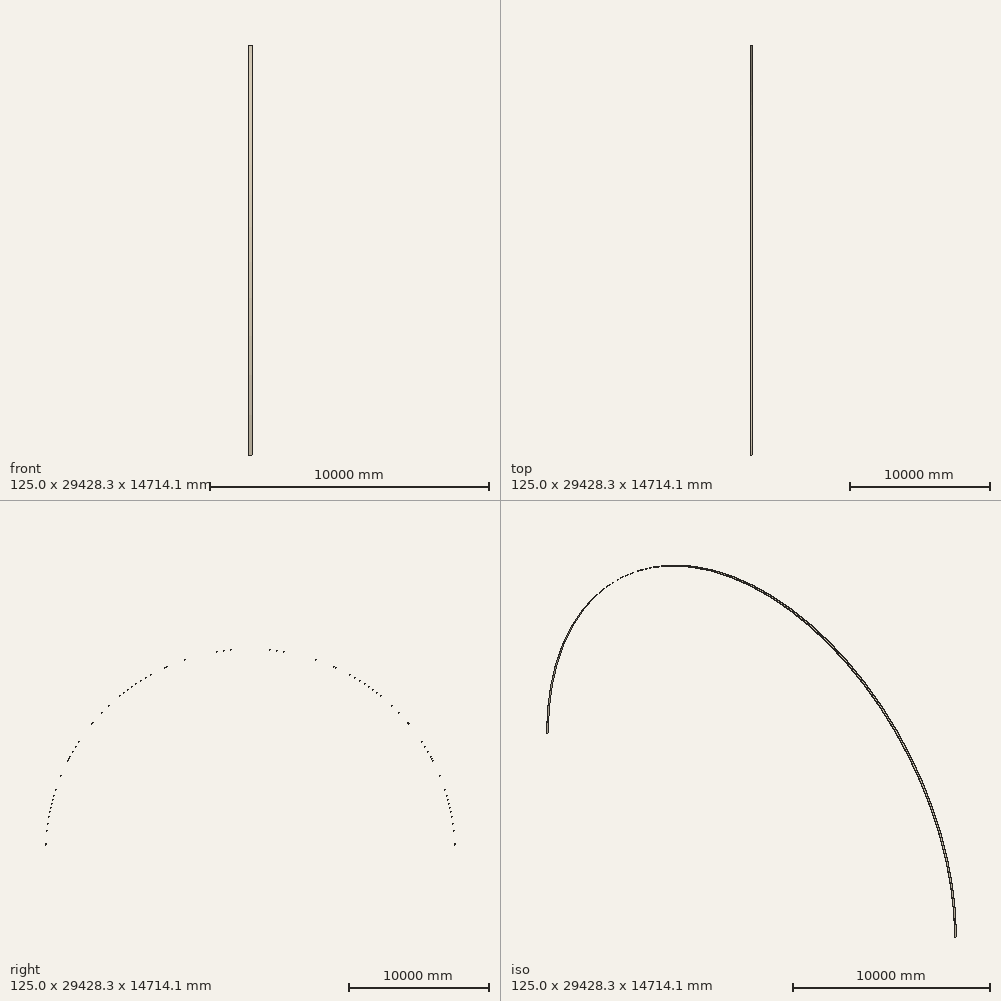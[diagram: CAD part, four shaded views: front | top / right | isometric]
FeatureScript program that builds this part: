
annotation { "Feature Type Name" : "Feature", "Feature Type Description" : "" }
export const myFeature = defineFeature(function(context is Context, id is Id, definition is map)
    precondition{}
    {
        {
            var Q0;
            Q0=qCreatedBy(makeId("Right.planeOp"),FACE);
            var sketch = newSketch(context, id + "F0", { "sketchPlane" : qUnion([Q0])});
            skLineSegment(sketch, "E0", {"start": v(14655.35, -4001.95) * mm, "end": v(14649.35, -4001.95) * mm});
            skArc(sketch, "E1", {"start": v(14655.35, -4001.95) * mm, "mid": v(-58.8, 10712.2) * mm, "end": v(-14772.93, -4001.95) * mm});
            skLineSegment(sketch, "E2", {"start": v(-14772.93, -4001.95) * mm, "end": v(-14766.93, -4001.95) * mm});
            skLineSegment(sketch, "E3", {"start": v(0, 10712.08) * mm, "end": v(0, 10706.08) * mm});
            skArc(sketch, "E4", {"start": v(14649.35, -4001.95) * mm, "mid": v(-58.8, 10706.2) * mm, "end": v(-14766.93, -4001.95) * mm});
            skLineSegment(sketch, "E5.trimOffspring", {"start": v(-14766.93, -4001.95) * mm, "end": v(-14772.93, -4001.95) * mm});
            skSolve(sketch);
        }
        {
            var Q0;
            Q0 = qSketchRegion(id + "F0", true);
            extrude(context, id + "F1", {"entities" : qUnion([Q0]), "depth" : 125 * mm});
        }
    });
